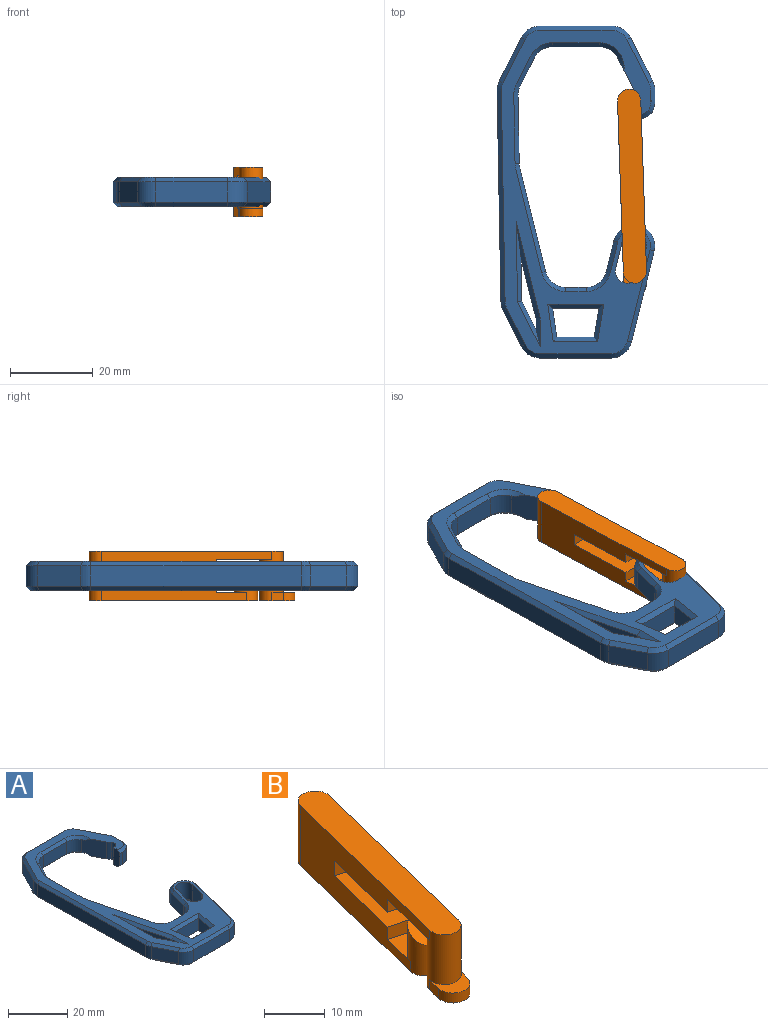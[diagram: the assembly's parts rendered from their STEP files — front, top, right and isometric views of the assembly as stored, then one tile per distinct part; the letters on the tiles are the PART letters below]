
ASSEMBLY  parts=2 mates=1
PART A: 130 faces, bbox 38.1x80.1x7.1 mm
  f0: plane 9x5mm, normal (0,1,0), area 45mm2, adj f1,f32,f82,f94
  f1: plane 7x5mm, normal (0.99,0.14,0), area 35.4mm2, adj f0,f2,f81,f93
  f2: plane 11.15x5mm, normal (0,-1,0), area 55.8mm2, adj f1,f32,f83,f95
  f3: plane 5x4.88mm, normal (0,1,0), area 24.4mm2, adj f35,f49,f59,f119
  f4: plane 24.96x6.24mm, normal (0.97,0.24,0), area 128.7mm2, adj f35,f36,f57,f121
  f5: plane 16.39x5mm, normal (1,0.02,0), area 81.9mm2, adj f36,f37,f55,f123
  f6: plane 6.65x5mm, normal (0.89,-0.45,0), area 37.3mm2, adj f37,f38,f53,f125
  f7: plane 11.23x5mm, normal (0,-1,0), area 56.1mm2, adj f38,f39,f51,f127
  f8: plane 7.82x7mm, normal (-0.89,-0.45,0), area 57mm2, adj f33,f34,f39,f50,f128,f129
  f9: cylinder r=1.5mm len=7mm, axis (0,0,-1), area 25mm2, adj f10,f33,f34,f129
  f10: plane 7x0.51mm, normal (0,1,0), area 3.6mm2, adj f9,f11,f33,f34
  f11: plane 7.04x3.04mm, normal (-1,0,0), area 19.9mm2, adj f10,f12,f33,f34,f80,f97
  f12: plane 5.09x1.2mm, normal (0,-1,0), area 5.5mm2, adj f11,f41,f80,f97
  f13: plane 5x0.25mm, normal (1,0,0), area 1.2mm2, adj f14,f40,f78,f100
  f14: plane 5x2.44mm, normal (1,-0.01,0), area 12.2mm2, adj f13,f42,f77,f101
  f15: plane 10.53x5.33mm, normal (0.89,0.45,0), area 59mm2, adj f42,f43,f75,f103
  f16: plane 17.37x5mm, normal (0,1,0), area 86.9mm2, adj f43,f44,f73,f105
  f17: plane 10.5x5.31mm, normal (-0.89,0.45,0), area 58.8mm2, adj f44,f45,f71,f107
  f18: plane 50.81x5mm, normal (-1,-0.02,0), area 254.1mm2, adj f45,f46,f69,f109
  f19: plane 8.69x5mm, normal (-0.89,-0.45,0), area 48.7mm2, adj f46,f47,f67,f111
  f20: plane 17.19x5mm, normal (0,-1,0), area 85.9mm2, adj f47,f48,f65,f113
  f21: plane 22x5.5mm, normal (0.97,-0.24,0), area 113.4mm2, adj f22,f48,f63,f115
  f22: cylinder r=5mm len=9.85mm, axis (0,0,-1), area 78.5mm2, adj f21,f29,f62,f116
  f23: plane 6.83x5mm, normal (0.89,0.45,0), area 38.3mm2, adj f24,f30,f87,f91
  f24: plane 10.39x5mm, normal (1,0.02,0), area 52mm2, adj f23,f25,f85,f89
  f25: plane 14.57x5mm, normal (-0.97,-0.24,0), area 75.1mm2, adj f24,f30,f86,f90
  f26: plane 7x6mm, normal (0.97,-0.24,0), area 43.3mm2, adj f27,f31,f33,f34
  f27: cylinder r=3mm len=7mm, axis (0,0,-1), area 66mm2, adj f26,f28,f33,f34
  f28: plane 7x6mm, normal (-0.97,0.24,0), area 43.3mm2, adj f27,f31,f33,f34
  f29: plane 7.43x5mm, normal (-0.97,0.24,0), area 38.3mm2, adj f22,f49,f61,f117
  f30: plane 5x2.65mm, normal (-1,0,0), area 13.3mm2, adj f23,f25,f88,f92
  f31: cylinder r=3mm len=7mm, axis (0,0,-1), area 66mm2, adj f26,f28,f33,f34
  f32: plane 7x5mm, normal (-0.99,0.16,0), area 35.5mm2, adj f0,f2,f84,f96
  f33: plane 78x36.01mm, normal (0,0,1), area 727.5mm2, adj f8,f9,f10,f11,f26,f27,f28,f31
  f34: plane 78x36.01mm, normal (0,0,-1), area 727.6mm2, adj f8,f9,f10,f11,f26,f27,f28,f31
  f35: cylinder r=5mm len=5mm, axis (0,0,1), area 33.1mm2, adj f3,f4,f58,f120
  f36: cylinder r=5mm len=5mm, axis (0,0,1), area 5.7mm2, adj f4,f5,f56,f122
  f37: cylinder r=5mm len=5mm, axis (0,0,-1), area 12.2mm2, adj f5,f6,f54,f124
  f38: cylinder r=5mm len=5mm, axis (0,0,-1), area 27.6mm2, adj f6,f7,f52,f126
  f39: cylinder r=5mm len=5mm, axis (0,0,1), area 27.6mm2, adj f7,f8,f50,f128
  f40: cylinder r=5mm len=5mm, axis (0,0,-1), area 14.5mm2, adj f13,f41,f79,f99
  f41: cylinder r=5mm len=5mm, axis (0,0,-1), area 20mm2, adj f12,f40,f80,f98
  f42: cylinder r=5mm len=5mm, axis (0,0,1), area 11.9mm2, adj f14,f15,f76,f102
  f43: cylinder r=5mm len=5mm, axis (0,0,1), area 27.6mm2, adj f15,f16,f74,f104
  f44: cylinder r=5mm len=5mm, axis (0,0,-1), area 27.6mm2, adj f16,f17,f72,f106
  f45: cylinder r=5mm len=5mm, axis (0,0,-1), area 12.2mm2, adj f17,f18,f70,f108
  f46: cylinder r=5mm len=5mm, axis (0,0,1), area 11.3mm2, adj f18,f19,f68,f110
  f47: cylinder r=5mm len=5mm, axis (0,0,-1), area 27.6mm2, adj f19,f20,f66,f112
  f48: cylinder r=5mm len=5mm, axis (0,0,1), area 33.1mm2, adj f20,f21,f64,f114
  f49: cylinder r=5mm len=5mm, axis (0,0,-1), area 33.1mm2, adj f3,f29,f60,f118
  f50: cone r=6mm half-angle=45deg, axis (0,0,1), area 11.8mm2, adj f8,f33,f39,f51
  f51: plane 11.23x1mm, normal (0,-0.71,0.71), area 15.9mm2, adj f7,f33,f50,f52
  f52: cone r=6mm half-angle=45deg, axis (0,0,1), area 8.6mm2, adj f33,f38,f51,f53
  f53: plane 7.1x4.26mm, normal (0.63,-0.32,0.71), area 10.5mm2, adj f6,f33,f52,f54
  f54: cone r=6mm half-angle=45deg, axis (0,0,1), area 3.8mm2, adj f33,f37,f53,f55
  f55: plane 16.41x1.3mm, normal (0.71,0.01,0.71), area 23.2mm2, adj f5,f33,f54,f56
  f56: cone r=6mm half-angle=45deg, axis (0,0,1), area 1.8mm2, adj f33,f36,f55,f57
  f57: plane 25.2x7.21mm, normal (0.69,0.17,0.71), area 36.4mm2, adj f4,f33,f56,f58
  f58: cone r=6mm half-angle=45deg, axis (0,0,1), area 10.3mm2, adj f33,f35,f57,f59
  f59: plane 4.88x1mm, normal (0,0.71,0.71), area 6.9mm2, adj f3,f33,f58,f60
  f60: cone r=6mm half-angle=45deg, axis (0,0,1), area 10.3mm2, adj f33,f49,f59,f61
  f61: plane 7.67x2.83mm, normal (-0.69,0.17,0.71), area 10.8mm2, adj f29,f33,f60,f62
  f62: cone r=4mm half-angle=45deg, axis (0,0,-1), area 20mm2, adj f22,f33,f61,f63
  f63: plane 22.24x6.47mm, normal (0.69,-0.17,0.71), area 32.1mm2, adj f21,f33,f62,f64
  f64: cone r=4mm half-angle=45deg, axis (0,0,-1), area 8.4mm2, adj f33,f48,f63,f65
  f65: plane 17.19x1mm, normal (0,-0.71,0.71), area 24.3mm2, adj f20,f33,f64,f66
  f66: cone r=4mm half-angle=45deg, axis (0,0,-1), area 7mm2, adj f33,f47,f65,f67
  f67: plane 9.14x5.29mm, normal (-0.63,-0.32,0.71), area 13.8mm2, adj f19,f33,f66,f68
  f68: cone r=4mm half-angle=45deg, axis (0,0,-1), area 2.9mm2, adj f33,f46,f67,f69
  f69: plane 50.83x1.92mm, normal (-0.71,-0.01,0.71), area 71.9mm2, adj f18,f33,f68,f70
  f70: cone r=4mm half-angle=45deg, axis (0,0,-1), area 3.1mm2, adj f33,f45,f69,f71
  f71: plane 10.95x6.21mm, normal (-0.63,0.32,0.71), area 16.6mm2, adj f17,f33,f70,f72
  f72: cone r=4mm half-angle=45deg, axis (0,0,-1), area 7mm2, adj f33,f44,f71,f73
  f73: plane 17.37x1mm, normal (0,0.71,0.71), area 24.6mm2, adj f16,f33,f72,f74
  f74: cone r=4mm half-angle=45deg, axis (0,0,-1), area 7mm2, adj f33,f43,f73,f75
  f75: plane 10.98x6.22mm, normal (0.63,0.32,0.71), area 16.7mm2, adj f15,f33,f74,f76
  f76: cone r=4mm half-angle=45deg, axis (0,0,-1), area 3mm2, adj f33,f42,f75,f77
  f77: plane 2.45x1.01mm, normal (0.71,0,0.71), area 3.5mm2, adj f14,f33,f76,f78
  f78: plane 1x1mm, normal (0.71,0,0.71), area 0.4mm2, adj f13,f33,f77,f79
  f79: cone r=4mm half-angle=45deg, axis (0,0,-1), area 3.6mm2, adj f33,f40,f78,f80
  f80: cone r=4mm half-angle=45deg, axis (0,0,-1), area 6.7mm2, adj f11,f12,f33,f41,f79
  f81: plane 9x2.16mm, normal (0.7,0.1,0.71), area 11.4mm2, adj f1,f33,f82,f83
  f82: plane 10.72x1mm, normal (0,0.71,0.71), area 13.9mm2, adj f0,f33,f81,f84
  f83: plane 13.49x1mm, normal (0,-0.71,0.71), area 17.4mm2, adj f2,f33,f81,f84
  f84: plane 9x2.33mm, normal (-0.7,0.11,0.71), area 11.5mm2, adj f32,f33,f82,f83
  f85: plane 19.4x1.35mm, normal (0.71,0.01,0.71), area 21.1mm2, adj f24,f33,f86,f87
  f86: plane 23.32x5.8mm, normal (-0.69,-0.17,0.71), area 27.5mm2, adj f25,f33,f85,f88
  f87: plane 11.02x5.45mm, normal (0.63,0.32,0.71), area 13.9mm2, adj f23,f33,f85,f88
  f88: plane 6.97x1mm, normal (-0.71,0,0.71), area 6.8mm2, adj f30,f33,f86,f87
  f89: plane 19.4x1.35mm, normal (0.71,0.01,-0.71), area 21.1mm2, adj f24,f34,f90,f91
  f90: plane 23.32x5.8mm, normal (-0.69,-0.17,-0.71), area 27.5mm2, adj f25,f34,f89,f92
  f91: plane 11.02x5.45mm, normal (0.63,0.32,-0.71), area 13.9mm2, adj f23,f34,f89,f92
  f92: plane 6.97x1mm, normal (-0.71,0,-0.71), area 6.8mm2, adj f30,f34,f90,f91
  f93: plane 9x2.16mm, normal (0.7,0.1,-0.71), area 11.4mm2, adj f1,f34,f94,f95
  f94: plane 10.72x1mm, normal (0,0.71,-0.71), area 13.9mm2, adj f0,f34,f93,f96
  f95: plane 13.49x1mm, normal (0,-0.71,-0.71), area 17.4mm2, adj f2,f34,f93,f96
  f96: plane 9x2.33mm, normal (-0.7,0.11,-0.71), area 11.5mm2, adj f32,f34,f94,f95
  f97: plane 1.11x1mm, normal (0,-0.71,-0.71), area 1.6mm2, adj f11,f12,f34,f98
  f98: cone r=4mm half-angle=45deg, axis (0,0,1), area 5mm2, adj f34,f41,f97,f99
  f99: cone r=4mm half-angle=45deg, axis (0,0,1), area 3.6mm2, adj f34,f40,f98,f100
  f100: plane 1x1mm, normal (0.71,0,-0.71), area 0.4mm2, adj f13,f34,f99,f101
  f101: plane 2.45x1.01mm, normal (0.71,0,-0.71), area 3.5mm2, adj f14,f34,f100,f102
  f102: cone r=4mm half-angle=45deg, axis (0,0,1), area 3mm2, adj f34,f42,f101,f103
  f103: plane 10.98x6.22mm, normal (0.63,0.32,-0.71), area 16.7mm2, adj f15,f34,f102,f104
  f104: cone r=4mm half-angle=45deg, axis (0,0,1), area 7mm2, adj f34,f43,f103,f105
  f105: plane 17.37x1mm, normal (0,0.71,-0.71), area 24.6mm2, adj f16,f34,f104,f106
  f106: cone r=4mm half-angle=45deg, axis (0,0,1), area 7mm2, adj f34,f44,f105,f107
  f107: plane 10.95x6.21mm, normal (-0.63,0.32,-0.71), area 16.6mm2, adj f17,f34,f106,f108
  f108: cone r=4mm half-angle=45deg, axis (0,0,1), area 3.1mm2, adj f34,f45,f107,f109
  f109: plane 50.83x1.92mm, normal (-0.71,-0.01,-0.71), area 71.9mm2, adj f18,f34,f108,f110
  f110: cone r=4mm half-angle=45deg, axis (0,0,1), area 2.9mm2, adj f34,f46,f109,f111
  f111: plane 9.14x5.29mm, normal (-0.63,-0.32,-0.71), area 13.8mm2, adj f19,f34,f110,f112
  f112: cone r=4mm half-angle=45deg, axis (0,0,1), area 7mm2, adj f34,f47,f111,f113
  f113: plane 17.19x1mm, normal (0,-0.71,-0.71), area 24.3mm2, adj f20,f34,f112,f114
  f114: cone r=4mm half-angle=45deg, axis (0,0,1), area 8.4mm2, adj f34,f48,f113,f115
  f115: plane 22.24x6.47mm, normal (0.69,-0.17,-0.71), area 32.1mm2, adj f21,f34,f114,f116
  f116: cone r=5mm half-angle=45deg, axis (0,0,1), area 20mm2, adj f22,f34,f115,f117
  f117: plane 7.67x2.83mm, normal (-0.69,0.17,-0.71), area 10.8mm2, adj f29,f34,f116,f118
  f118: cone r=6mm half-angle=45deg, axis (0,0,-1), area 10.3mm2, adj f34,f49,f117,f119
  f119: plane 4.88x1mm, normal (0,0.71,-0.71), area 6.9mm2, adj f3,f34,f118,f120
  f120: cone r=6mm half-angle=45deg, axis (0,0,-1), area 10.3mm2, adj f34,f35,f119,f121
  f121: plane 25.2x7.21mm, normal (0.69,0.17,-0.71), area 36.4mm2, adj f4,f34,f120,f122
  f122: cone r=6mm half-angle=45deg, axis (0,0,-1), area 1.8mm2, adj f34,f36,f121,f123
  f123: plane 16.41x1.3mm, normal (0.71,0.01,-0.71), area 23.2mm2, adj f5,f34,f122,f124
  f124: cone r=6mm half-angle=45deg, axis (0,0,-1), area 3.8mm2, adj f34,f37,f123,f125
  f125: plane 7.1x4.26mm, normal (0.63,-0.32,-0.71), area 10.5mm2, adj f6,f34,f124,f126
  f126: cone r=6mm half-angle=45deg, axis (0,0,-1), area 8.6mm2, adj f34,f38,f125,f127
  f127: plane 11.23x1mm, normal (0,-0.71,-0.71), area 15.9mm2, adj f7,f34,f126,f128
  f128: cone r=6mm half-angle=45deg, axis (0,0,-1), area 11.8mm2, adj f8,f34,f39,f127
  f129: cylinder r=5mm len=7mm, axis (0,0,-1), area 11.9mm2, adj f8,f9,f33,f34
PART B: 27 faces, bbox 16.3x48.3x12 mm
  f0: plane 5.43x2.5mm, normal (-0.24,-0.97,0), area 14mm2, adj f1,f2,f12,f24
  f1: plane 39.96x12mm, normal (0.97,-0.24,0), area 284.6mm2, adj f0,f3,f4,f5,f6,f12,f13,f14
  f2: plane 39.96x12mm, normal (-0.97,0.24,0), area 324.2mm2, adj f0,f4,f6,f12,f13,f14,f16,f17
  f3: plane 8.27x4.7mm, normal (0,0,1), area 20.4mm2, adj f1,f13,f15,f18,f20,f21,f22
  f4: plane 8.29x7.17mm, normal (0,0,1), area 27.7mm2, adj f1,f2,f16,f19
  f5: plane 8.27x4.7mm, normal (0,0,-1), area 20.4mm2, adj f1,f13,f15,f18,f20,f21,f22
  f6: cylinder r=2.8mm len=12mm, axis (0,0,-1), area 175.9mm2, adj f1,f2,f7,f8,f10,f11,f12,f14
  f7: plane 2.72x2mm, normal (-0.97,0.24,0), area 5.6mm2, adj f6,f9,f10,f11
  f8: plane 2.72x2mm, normal (0.97,-0.24,0), area 5.6mm2, adj f6,f9,f10,f11
  f9: cylinder r=2.8mm len=5.52mm, axis (0,0,1), area 17.6mm2, adj f7,f8,f10,f11
  f10: plane 8.32x6.28mm, normal (0,0,-1), area 40.3mm2, adj f6,f7,f8,f9
  f11: plane 6.2x6.2mm, normal (0,0,1), area 15.7mm2, adj f6,f7,f8,f9
  f12: plane 14.29x8.67mm, normal (0,0,-1), area 62.3mm2, adj f0,f1,f2,f6
  f13: cylinder r=2.8mm len=12mm, axis (0,0,-1), area 67.5mm2, adj f1,f2,f3,f5,f14,f17,f18
  f14: plane 45.56x15.59mm, normal (0,0,1), area 255.3mm2, adj f1,f2,f6,f13
  f15: cylinder r=1.3mm len=8mm, axis (0,0,-1), area 33.5mm2, adj f3,f5,f18,f22
  f16: cylinder r=2.8mm len=9mm, axis (0,0,1), area 114.5mm2, adj f1,f2,f4,f17,f23
  f17: plane 39.56x14.09mm, normal (0,0,-1), area 220.6mm2, adj f1,f2,f13,f16
  f18: plane 8x1.5mm, normal (1,-0.08,0), area 12mm2, adj f3,f5,f13,f15
  f19: plane 5.43x2.5mm, normal (-0.24,-0.97,0), area 14mm2, adj f1,f2,f4,f25
  f20: plane 8x3.41mm, normal (0.24,0.97,0), area 28.2mm2, adj f1,f3,f5,f21
  f21: plane 8x3.55mm, normal (0.97,-0.24,0), area 29.2mm2, adj f3,f5,f20,f22
  f22: plane 8x0.7mm, normal (-0.24,-0.97,0), area 5.8mm2, adj f3,f5,f15,f21
  f23: plane 5.61x5.61mm, normal (-0.11,-0.46,0.88), area 27.9mm2, adj f16
  f24: plane 17.85x9.56mm, normal (0,0,-1), area 95.2mm2, adj f0,f1,f2,f26
  f25: plane 17.85x9.56mm, normal (0,0,1), area 95.2mm2, adj f1,f2,f19,f26
  f26: plane 5.43x3mm, normal (-0.24,-0.97,0), area 16.8mm2, adj f1,f2,f24,f25
PLACE A at identity fixed
PLACE B rot(axis=(0,0,1),16deg) t=(-3.04,-4.35,0)mm
MATE revolute A.f22 <-> B.f16  axis (0,0,-1) through (14,-13,0)mm
